# Revit family: Hager-Pedro-vuoto-NoHosted-IT-it
name_source: partatom
category: Electrical Equipment
units: mm (PartAtom-declared; Revit-internal decimal feet)

## family parameters
Always vertical = Yes
Cut with Voids When Loaded = No
Panel Configuration = Two Columns, Circuits Across
Part Type = Panelboard
Room Calculation Point = No
Round Connector Dimension = Use Diameter
Shared = No
Work Plane-Based = Yes

## types (2) — shared parameters
Default Elevation = 1219 mm
EF000003 - Tipo di montaggio = EV000384 - A parete
EF000007 - colore = EV000270 - grigio
EF000008 - Larghezza = 265 mm  [stored 0.869423 ft]
EF000040 - Altezza = 303 mm  [stored 0.994094 ft]
EF000049 - profondità = 167 mm  [stored 0.5479 ft]
EF000116 - numero RAL = 7035
EF000118 - con piastra di montaggio = No
EF000339 - tipo di copertura = EV004216 - porta
EF001062 - esecuzione EMC = Yes
EF001088 - possibilità di applicazione = Yes
EF001131 - profondità interna = 137 mm
EF001134 - barra DIN = No
EF001596 - Attacco Lampada = EV000139 - plastica
EF004462 - tipo di chiusura = EV000154 - altri
EF005474 - grado di protezione (IP) = EV006422 - IP66
EF006306 - con serratura = Yes
EF009212 - esecuzione coperchio = EV000116 - chiuso
EF015776 - Morsettiera di terra = No
EF015777 - Morsettiera neutra = No
EF015941 - Segnale di passaggio porta = No
HG000002 - Con porta = Yes
HG000003 - Gamma = Pedro
HG000005 - Spessore = 3 mm  [stored 0.00984252 ft]
HG000006 - Ad incasso = No
HG000009 - Porta doppia a battente = No
HG000010 - Porte asimmetriche = No
HG000011 - File vuote nella parte basse = No
HG000017 - Distanza tra i poli = 18 mm  [stored 0.0590551 ft]
Manufacturer = Hager
Type Comments = Pedro
zero-valued in all types: EF000218 - profondità di incasso, EF000266 - numero di file, EF000332 - Altezza della parte incassata, EF000846 - larghezza di montaggio, EF002950 - Numero moduli DIN, HG000001 - Numero di colonne, HG000007 - Numero di colonne vuote, HG000008 - Numero di file vuote

## per-type parameters (varying)
| type | EF006244 - coperchio/porta trasparente | HG000004 - Codice produttore | Model |
| A parete IP66 L264.7 A302.8 P167  Unità di divisione - B04601 | No | B04601 | B04601 |
| A parete IP66 L264.7 A302.8 P167  Unità di divisione - B04621 | Yes | B04621 | B04621 |

note: [stored X ft] marks values corroborated as IEEE doubles in the binary element streams (Revit-internal decimal feet)

## geometry (parser evidence)
native form markers: Sweep x13
no freeform markers — native parametric forms only
